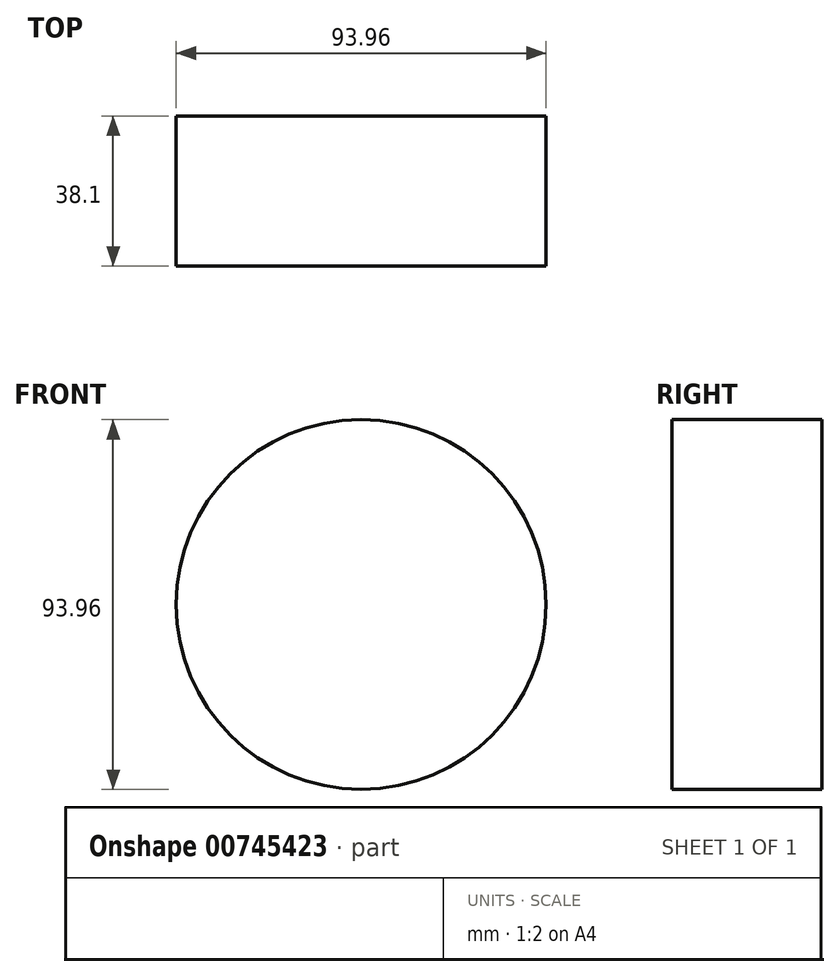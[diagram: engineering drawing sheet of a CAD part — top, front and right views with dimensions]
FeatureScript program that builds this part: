
annotation { "Feature Type Name" : "Feature", "Feature Type Description" : "" }
export const myFeature = defineFeature(function(context is Context, id is Id, definition is map)
    precondition{}
    {
        {
            var Q0;
            Q0=qCreatedBy(makeId("Front.planeOp"),FACE);
            var sketch = newSketch(context, id + "F0", { "sketchPlane" : qUnion([Q0])});
            skCircle(sketch, "E0", {"center": v(0, 0) * mm, "radius": 46.98 * mm});
            skSolve(sketch);
        }
        {
            var Q0;
            Q0=makeQuery(id+"F0.imprint","IMPRINT",FACE,{"disambiguationData":[TD([[makeQuery(id+"F0.imprint","IMPRINT",EDGE,{"derivedFrom":sQuery(id+"F0.wireOp",EDGE,"E0")}),1.0]])]});
            var Q1;
            Q1=sQuery(id+"F0.wireOp",EDGE,"E0");
            extrude(context, id + "F1", {"entities" : qUnion([Q0]), "surfaceEntities" : qUnion([Q1]), "depth" : 38.1 * mm, "offsetDistance" : 25.4 * mm});
        }
    });
